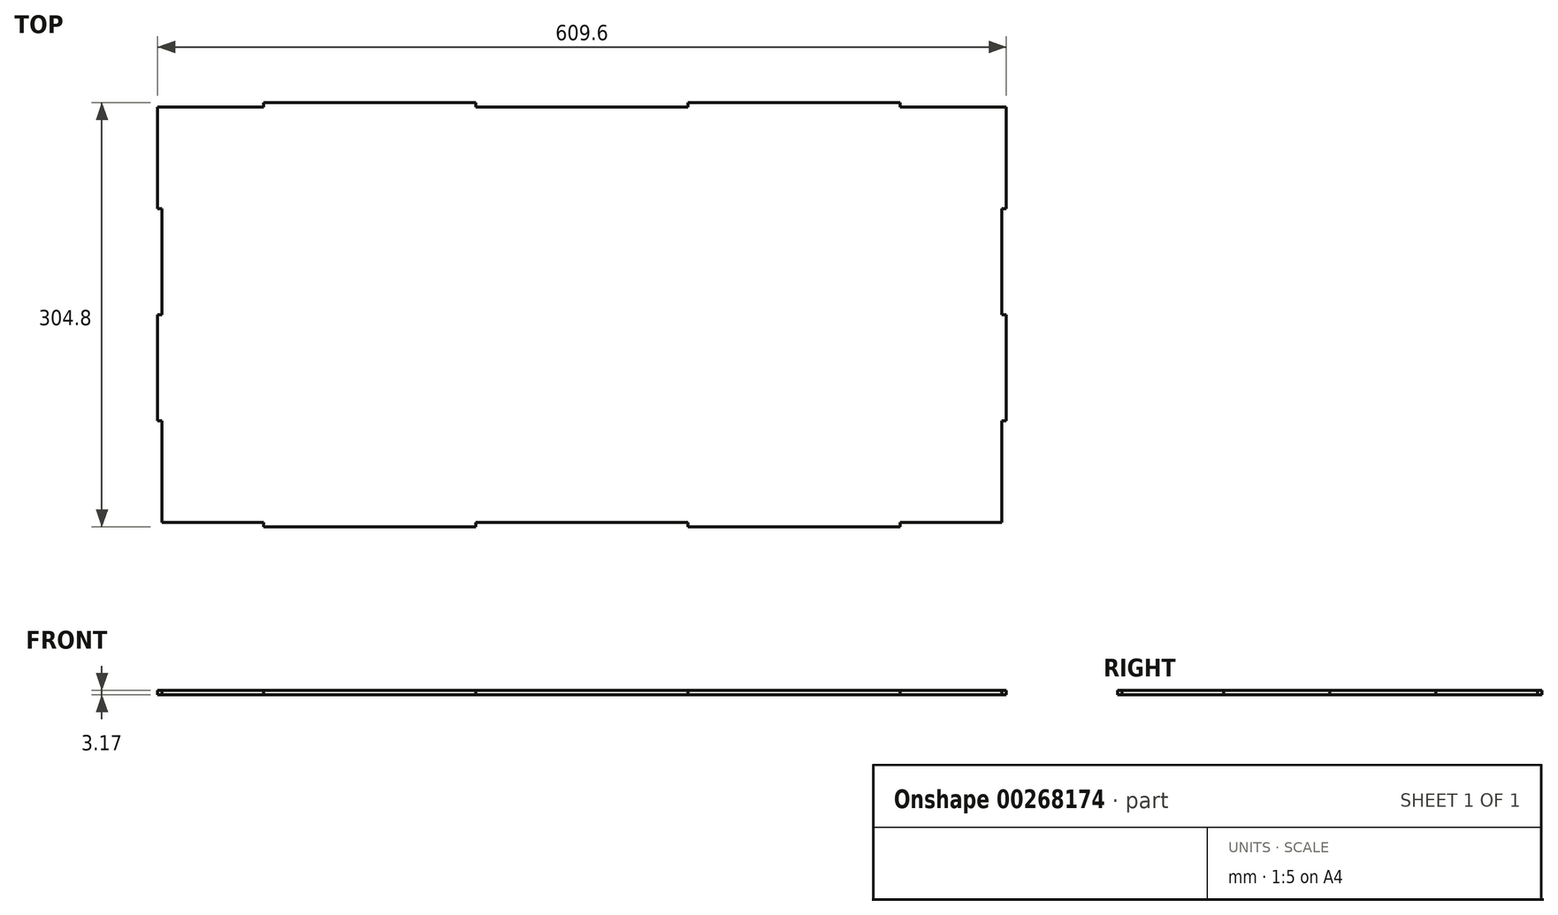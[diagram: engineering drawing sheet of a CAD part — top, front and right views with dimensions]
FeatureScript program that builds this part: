
annotation { "Feature Type Name" : "Feature", "Feature Type Description" : "" }
export const myFeature = defineFeature(function(context is Context, id is Id, definition is map)
    precondition{}
    {
        {
            var Q0;
            Q0=qCreatedBy(makeId("Top.planeOp"),FACE);
            var sketch = newSketch(context, id + "F0", { "sketchPlane" : qUnion([Q0])});
            skLineSegment(sketch, "E0.bottom", {"start": v(-219.98, 153.82) * mm, "end": v(389.62, 153.82) * mm});
            skLineSegment(sketch, "E0.top", {"start": v(-219.98, -150.98) * mm, "end": v(389.62, -150.98) * mm});
            skLineSegment(sketch, "E0.left", {"start": v(-219.98, 153.82) * mm, "end": v(-219.98, -150.98) * mm});
            skLineSegment(sketch, "E0.right", {"start": v(389.62, 153.82) * mm, "end": v(389.62, -150.98) * mm});
            skSolve(sketch);
        }
        {
            var Q0;
            Q0 = qSketchRegion(id + "F0", true);
            extrude(context, id + "F1", {"entities" : qUnion([Q0]), "depth" : 3.17 * mm});
        }
        {
            var Q0;
            Q0=makeQuery(id+"F1.opExtrude","CAP_FACE",FACE,{"disambiguationData":[OSD([sQuery(id+"F0.wireOp",EDGE,"E0.bottom"),sQuery(id+"F0.wireOp",EDGE,"E0.top"),sQuery(id+"F0.wireOp",EDGE,"E0.left"),sQuery(id+"F0.wireOp",EDGE,"E0.right")])],"isStart":false});
            var sketch = newSketch(context, id + "F2", { "sketchPlane" : qUnion([Q0])});
            skLineSegment(sketch, "E1.bottom", {"start": v(-219.98, 153.82) * mm, "end": v(-143.78, 153.82) * mm});
            skLineSegment(sketch, "E1.top", {"start": v(-219.98, 150.65) * mm, "end": v(-143.78, 150.65) * mm});
            skLineSegment(sketch, "E1.left", {"start": v(-219.98, 153.82) * mm, "end": v(-219.98, 150.65) * mm});
            skLineSegment(sketch, "E1.right", {"start": v(-143.78, 153.82) * mm, "end": v(-143.78, 150.65) * mm});
            skLineSegment(sketch, "E2.bottom", {"start": v(-143.78, 153.82) * mm, "end": v(-67.58, 153.82) * mm});
            skLineSegment(sketch, "E2.top", {"start": v(-143.78, 150.65) * mm, "end": v(-67.58, 150.65) * mm});
            skLineSegment(sketch, "E2.right", {"start": v(-67.58, 153.82) * mm, "end": v(-67.58, 150.65) * mm});
            skLineSegment(sketch, "E3.bottom", {"start": v(-67.58, 153.82) * mm, "end": v(8.62, 153.82) * mm});
            skLineSegment(sketch, "E3.top", {"start": v(-67.58, 150.65) * mm, "end": v(8.62, 150.65) * mm});
            skLineSegment(sketch, "E3.right", {"start": v(8.62, 153.82) * mm, "end": v(8.62, 150.65) * mm});
            skLineSegment(sketch, "E4.bottom", {"start": v(8.62, 153.82) * mm, "end": v(84.82, 153.82) * mm});
            skLineSegment(sketch, "E4.top", {"start": v(8.62, 150.65) * mm, "end": v(84.82, 150.65) * mm});
            skLineSegment(sketch, "E4.right", {"start": v(84.82, 153.82) * mm, "end": v(84.82, 150.65) * mm});
            skLineSegment(sketch, "E5.bottom", {"start": v(84.82, 153.82) * mm, "end": v(161.02, 153.82) * mm});
            skLineSegment(sketch, "E5.top", {"start": v(84.82, 150.65) * mm, "end": v(161.02, 150.65) * mm});
            skLineSegment(sketch, "E5.right", {"start": v(161.02, 153.82) * mm, "end": v(161.02, 150.65) * mm});
            skLineSegment(sketch, "E6.bottom", {"start": v(161.02, 153.82) * mm, "end": v(237.22, 153.82) * mm});
            skLineSegment(sketch, "E6.top", {"start": v(161.02, 150.65) * mm, "end": v(237.22, 150.65) * mm});
            skLineSegment(sketch, "E6.right", {"start": v(237.22, 153.82) * mm, "end": v(237.22, 150.65) * mm});
            skLineSegment(sketch, "E7.bottom", {"start": v(237.22, 153.82) * mm, "end": v(313.42, 153.82) * mm});
            skLineSegment(sketch, "E7.top", {"start": v(237.22, 150.65) * mm, "end": v(313.42, 150.65) * mm});
            skLineSegment(sketch, "E7.right", {"start": v(313.42, 153.82) * mm, "end": v(313.42, 150.65) * mm});
            skLineSegment(sketch, "E8.bottom", {"start": v(313.42, 153.82) * mm, "end": v(389.62, 153.82) * mm});
            skLineSegment(sketch, "E8.top", {"start": v(313.42, 150.65) * mm, "end": v(389.62, 150.65) * mm});
            skLineSegment(sketch, "E8.right", {"start": v(389.62, 153.82) * mm, "end": v(389.62, 150.65) * mm});
            skLineSegment(sketch, "E9.bottom", {"start": v(-219.98, -147.8) * mm, "end": v(-143.78, -147.8) * mm});
            skLineSegment(sketch, "E9.top", {"start": v(-219.98, -150.98) * mm, "end": v(-143.78, -150.98) * mm});
            skLineSegment(sketch, "E9.left", {"start": v(-219.98, -147.8) * mm, "end": v(-219.98, -150.98) * mm});
            skLineSegment(sketch, "E9.right", {"start": v(-143.78, -147.8) * mm, "end": v(-143.78, -150.98) * mm});
            skLineSegment(sketch, "E10.bottom", {"start": v(-143.78, -147.8) * mm, "end": v(-67.58, -147.8) * mm});
            skLineSegment(sketch, "E10.top", {"start": v(-143.78, -150.98) * mm, "end": v(-67.58, -150.98) * mm});
            skLineSegment(sketch, "E10.right", {"start": v(-67.58, -147.8) * mm, "end": v(-67.58, -150.98) * mm});
            skLineSegment(sketch, "E11.bottom", {"start": v(-67.58, -147.8) * mm, "end": v(8.62, -147.8) * mm});
            skLineSegment(sketch, "E11.top", {"start": v(-67.58, -150.98) * mm, "end": v(8.62, -150.98) * mm});
            skLineSegment(sketch, "E11.right", {"start": v(8.62, -147.8) * mm, "end": v(8.62, -150.98) * mm});
            skLineSegment(sketch, "E12.bottom", {"start": v(8.62, -147.8) * mm, "end": v(84.82, -147.8) * mm});
            skLineSegment(sketch, "E12.top", {"start": v(8.62, -150.98) * mm, "end": v(84.82, -150.98) * mm});
            skLineSegment(sketch, "E12.right", {"start": v(84.82, -147.8) * mm, "end": v(84.82, -150.98) * mm});
            skLineSegment(sketch, "E13.bottom", {"start": v(84.82, -147.8) * mm, "end": v(161.02, -147.8) * mm});
            skLineSegment(sketch, "E13.top", {"start": v(84.82, -150.98) * mm, "end": v(161.02, -150.98) * mm});
            skLineSegment(sketch, "E13.right", {"start": v(161.02, -147.8) * mm, "end": v(161.02, -150.98) * mm});
            skLineSegment(sketch, "E14.bottom", {"start": v(161.02, -147.8) * mm, "end": v(237.22, -147.8) * mm});
            skLineSegment(sketch, "E14.top", {"start": v(161.02, -150.98) * mm, "end": v(237.22, -150.98) * mm});
            skLineSegment(sketch, "E14.right", {"start": v(237.22, -147.8) * mm, "end": v(237.22, -150.98) * mm});
            skLineSegment(sketch, "E15.bottom", {"start": v(237.22, -147.8) * mm, "end": v(313.42, -147.8) * mm});
            skLineSegment(sketch, "E15.top", {"start": v(237.22, -150.98) * mm, "end": v(313.42, -150.98) * mm});
            skLineSegment(sketch, "E15.right", {"start": v(313.42, -147.8) * mm, "end": v(313.42, -150.98) * mm});
            skLineSegment(sketch, "E16.bottom", {"start": v(313.42, -147.8) * mm, "end": v(389.62, -147.8) * mm});
            skLineSegment(sketch, "E16.top", {"start": v(313.42, -150.98) * mm, "end": v(389.62, -150.98) * mm});
            skLineSegment(sketch, "E16.right", {"start": v(389.62, -147.8) * mm, "end": v(389.62, -150.98) * mm});
            skSolve(sketch);
        }
        {
            var Q0;
            Q0=makeQuery(id+"F2.imprint","IMPRINT",FACE,{"disambiguationData":[TD([[makeQuery(id+"F2.imprint","IMPRINT",EDGE,{"derivedFrom":sQuery(id+"F2.wireOp",EDGE,"E1.bottom")}),-1.0]])]});
            var Q1;
            Q1=makeQuery(id+"F2.imprint","IMPRINT",FACE,{"disambiguationData":[TD([[makeQuery(id+"F2.imprint","IMPRINT",EDGE,{"derivedFrom":sQuery(id+"F2.wireOp",EDGE,"E8.bottom")}),-1.0]])]});
            var Q2;
            Q2=makeQuery(id+"F2.imprint","IMPRINT",FACE,{"disambiguationData":[TD([[makeQuery(id+"F2.imprint","IMPRINT",EDGE,{"derivedFrom":sQuery(id+"F2.wireOp",EDGE,"E9.bottom")}),-1.0]])]});
            var Q3;
            Q3=makeQuery(id+"F2.imprint","IMPRINT",FACE,{"disambiguationData":[TD([[makeQuery(id+"F2.imprint","IMPRINT",EDGE,{"derivedFrom":sQuery(id+"F2.wireOp",EDGE,"E16.bottom")}),-1.0]])]});
            var Q4;
            Q4=makeQuery(id+"F2.imprint","IMPRINT",FACE,{"disambiguationData":[TD([[makeQuery(id+"F2.imprint","IMPRINT",EDGE,{"derivedFrom":sQuery(id+"F2.wireOp",EDGE,"E4.bottom")}),-1.0]])]});
            var Q5;
            Q5=makeQuery(id+"F2.imprint","IMPRINT",FACE,{"disambiguationData":[TD([[makeQuery(id+"F2.imprint","IMPRINT",EDGE,{"derivedFrom":sQuery(id+"F2.wireOp",EDGE,"E5.bottom")}),-1.0]])]});
            var Q6;
            Q6=makeQuery(id+"F2.imprint","IMPRINT",FACE,{"disambiguationData":[TD([[makeQuery(id+"F2.imprint","IMPRINT",EDGE,{"derivedFrom":sQuery(id+"F2.wireOp",EDGE,"E12.bottom")}),-1.0]])]});
            var Q7;
            Q7=makeQuery(id+"F2.imprint","IMPRINT",FACE,{"disambiguationData":[TD([[makeQuery(id+"F2.imprint","IMPRINT",EDGE,{"derivedFrom":sQuery(id+"F2.wireOp",EDGE,"E13.bottom")}),-1.0]])]});
            extrude(context, id + "F3", {"entities" : qUnion([Q0, Q1, Q2, Q3, Q4, Q5, Q6, Q7]), "operationType" : NewBodyOperationType.REMOVE, "endBound" : BoundingType.THROUGH_ALL, "oppositeDirection" : true, "depth" : 3.17 * mm});
        }
        {
            var Q0;
            Q0=makeQuery(id+"F1.opExtrude","CAP_FACE",FACE,{"disambiguationData":[OSD([sQuery(id+"F0.wireOp",EDGE,"E0.bottom"),sQuery(id+"F0.wireOp",EDGE,"E0.top"),sQuery(id+"F0.wireOp",EDGE,"E0.left"),sQuery(id+"F0.wireOp",EDGE,"E0.right")])],"isStart":false});
            var sketch = newSketch(context, id + "F4", { "sketchPlane" : qUnion([Q0])});
            skLineSegment(sketch, "E17.bottom", {"start": v(-219.98, 150.65) * mm, "end": v(-216.8, 150.65) * mm});
            skLineSegment(sketch, "E17.top", {"start": v(-219.98, 77.62) * mm, "end": v(-216.8, 77.62) * mm});
            skLineSegment(sketch, "E17.left", {"start": v(-219.98, 150.65) * mm, "end": v(-219.98, 77.62) * mm});
            skLineSegment(sketch, "E17.right", {"start": v(-216.8, 150.65) * mm, "end": v(-216.8, 77.62) * mm});
            skLineSegment(sketch, "E18.bottom", {"start": v(-219.98, -74.78) * mm, "end": v(-216.8, -74.78) * mm});
            skLineSegment(sketch, "E18.top", {"start": v(-219.98, -147.8) * mm, "end": v(-216.8, -147.8) * mm});
            skLineSegment(sketch, "E18.left", {"start": v(-219.98, -74.78) * mm, "end": v(-219.98, -147.8) * mm});
            skLineSegment(sketch, "E18.right", {"start": v(-216.8, -74.78) * mm, "end": v(-216.8, -147.8) * mm});
            skLineSegment(sketch, "E19.top", {"start": v(-219.98, 1.42) * mm, "end": v(-216.8, 1.42) * mm});
            skLineSegment(sketch, "E19.left", {"start": v(-219.98, 77.62) * mm, "end": v(-219.98, 1.42) * mm});
            skLineSegment(sketch, "E19.right", {"start": v(-216.8, 77.62) * mm, "end": v(-216.8, 1.42) * mm});
            skLineSegment(sketch, "E20.left", {"start": v(-219.98, 1.42) * mm, "end": v(-219.98, -74.78) * mm});
            skLineSegment(sketch, "E20.right", {"start": v(-216.8, 1.42) * mm, "end": v(-216.8, -74.78) * mm});
            skLineSegment(sketch, "E21.bottom", {"start": v(389.62, -147.8) * mm, "end": v(386.45, -147.8) * mm});
            skLineSegment(sketch, "E21.top", {"start": v(389.62, -74.78) * mm, "end": v(386.45, -74.78) * mm});
            skLineSegment(sketch, "E21.left", {"start": v(389.62, -147.8) * mm, "end": v(389.62, -74.78) * mm});
            skLineSegment(sketch, "E21.right", {"start": v(386.45, -147.8) * mm, "end": v(386.45, -74.78) * mm});
            skLineSegment(sketch, "E22.bottom", {"start": v(386.45, -74.78) * mm, "end": v(389.62, -74.78) * mm});
            skLineSegment(sketch, "E22.top", {"start": v(386.45, 1.42) * mm, "end": v(389.62, 1.42) * mm});
            skLineSegment(sketch, "E22.left", {"start": v(386.45, -74.78) * mm, "end": v(386.45, 1.42) * mm});
            skLineSegment(sketch, "E22.right", {"start": v(389.62, -74.78) * mm, "end": v(389.62, 1.42) * mm});
            skLineSegment(sketch, "E23.top", {"start": v(386.45, 77.62) * mm, "end": v(389.62, 77.62) * mm});
            skLineSegment(sketch, "E23.left", {"start": v(386.45, 1.42) * mm, "end": v(386.45, 77.62) * mm});
            skLineSegment(sketch, "E23.right", {"start": v(389.62, 1.42) * mm, "end": v(389.62, 77.62) * mm});
            skLineSegment(sketch, "E24.bottom", {"start": v(389.62, 77.62) * mm, "end": v(386.45, 77.62) * mm});
            skLineSegment(sketch, "E24.top", {"start": v(389.62, 150.65) * mm, "end": v(386.45, 150.65) * mm});
            skLineSegment(sketch, "E24.left", {"start": v(389.62, 77.62) * mm, "end": v(389.62, 150.65) * mm});
            skLineSegment(sketch, "E24.right", {"start": v(386.45, 77.62) * mm, "end": v(386.45, 150.65) * mm});
            skSolve(sketch);
        }
        {
            var Q0;
            Q0=makeQuery(id+"F4.imprint","IMPRINT",FACE,{"disambiguationData":[TD([[makeQuery(id+"F4.imprint","IMPRINT",EDGE,{"derivedFrom":sQuery(id+"F4.wireOp",EDGE,"E22.top")}),1.0]])]});
            var Q1;
            Q1=makeQuery(id+"F4.imprint","IMPRINT",FACE,{"disambiguationData":[TD([[makeQuery(id+"F4.imprint","IMPRINT",EDGE,{"derivedFrom":sQuery(id+"F4.wireOp",EDGE,"E21.bottom")}),1.0]])]});
            var Q2;
            Q2=makeQuery(id+"F4.imprint","IMPRINT",FACE,{"disambiguationData":[TD([[makeQuery(id+"F4.imprint","IMPRINT",EDGE,{"derivedFrom":sQuery(id+"F4.wireOp",EDGE,"E18.top")}),1.0]])]});
            var Q3;
            Q3=makeQuery(id+"F4.imprint","IMPRINT",FACE,{"disambiguationData":[TD([[makeQuery(id+"F4.imprint","IMPRINT",EDGE,{"derivedFrom":sQuery(id+"F4.wireOp",EDGE,"E17.top")}),-1.0]])]});
            extrude(context, id + "F5", {"entities" : qUnion([Q0, Q1, Q2, Q3]), "operationType" : NewBodyOperationType.REMOVE, "endBound" : BoundingType.THROUGH_ALL, "oppositeDirection" : true, "depth" : 25.4 * mm});
        }
    });
